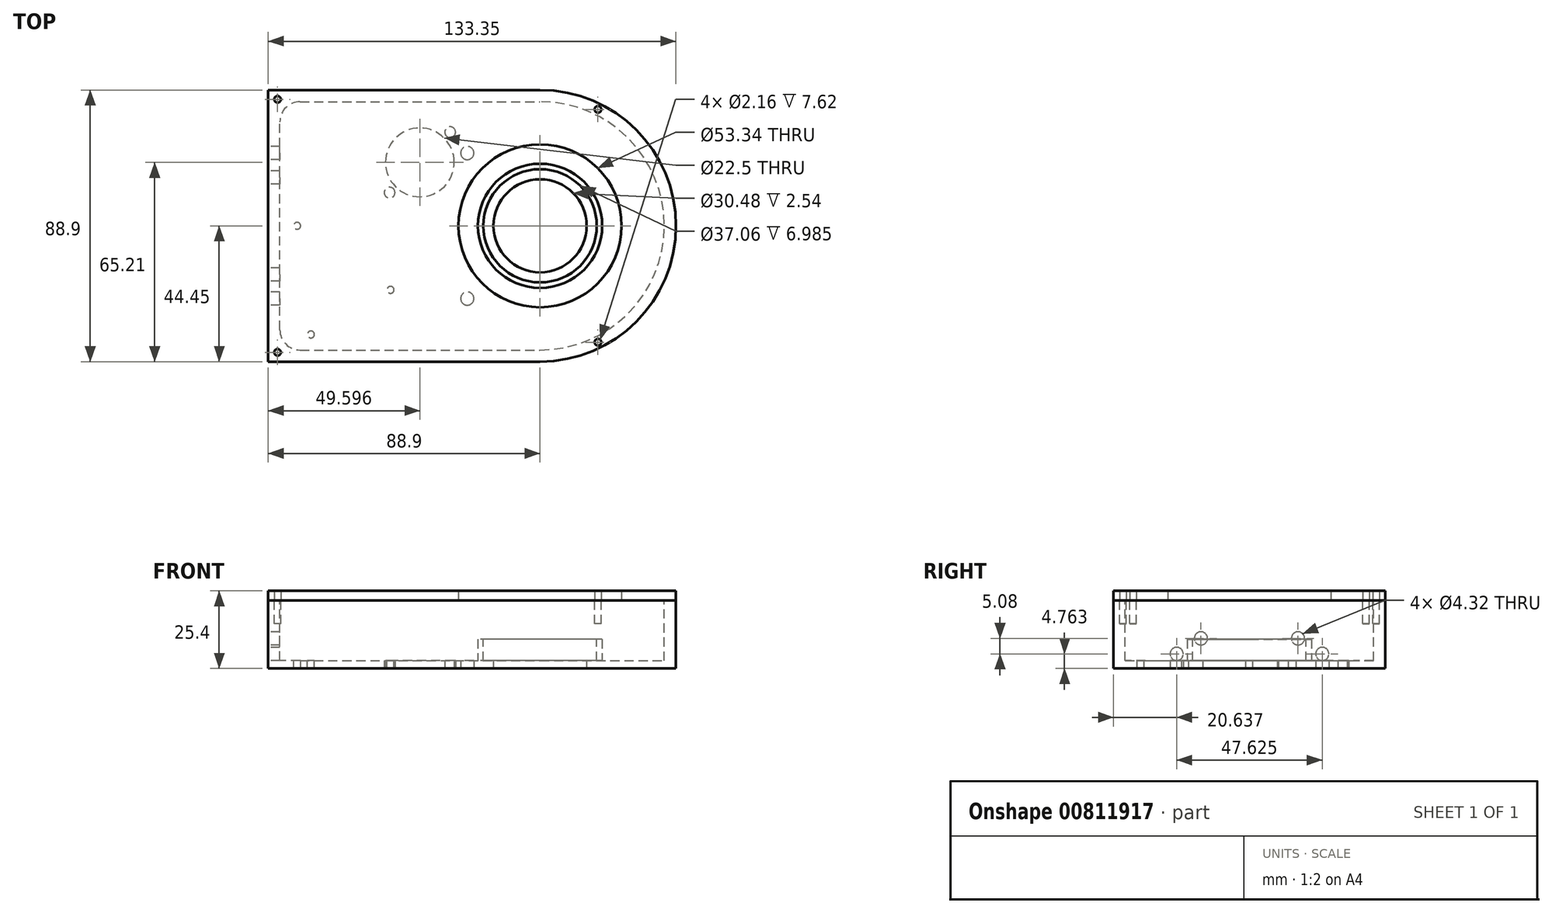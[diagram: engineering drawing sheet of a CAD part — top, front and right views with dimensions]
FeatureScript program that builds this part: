
annotation { "Feature Type Name" : "Feature", "Feature Type Description" : "" }
export const myFeature = defineFeature(function(context is Context, id is Id, definition is map)
    precondition{}
    {
        {
            var Q0;
            Q0=qCreatedBy(makeId("Top.planeOp"),FACE);
            var sketch = newSketch(context, id + "F0", { "sketchPlane" : qUnion([Q0])});
            skLineSegment(sketch, "E0.bottom", {"start": v(0, 0) * mm, "end": v(88.9, 0) * mm});
            skLineSegment(sketch, "E0.top", {"start": v(0, 88.9) * mm, "end": v(88.9, 88.9) * mm});
            skLineSegment(sketch, "E0.left", {"start": v(0, 0) * mm, "end": v(0, 88.9) * mm});
            skLineSegment(sketch, "E0.right", {"start": v(88.9, 0) * mm, "end": v(88.9, 88.9) * mm});
            skArc(sketch, "E1", {"start": v(88.9, 0) * mm, "mid": v(133.35, 44.45) * mm, "end": v(88.9, 88.9) * mm});
            skCircle(sketch, "E2", {"center": v(88.9, 44.45) * mm, "radius": 15.24 * mm});
            skCircle(sketch, "E3", {"center": v(88.9, 44.45) * mm, "radius": 31.75 * mm, "construction": true});
            skCircle(sketch, "E4", {"center": v(49.6, 65.21) * mm, "radius": 12.7 * mm, "construction": true});
            skCircle(sketch, "E5", {"center": v(49.6, 65.21) * mm, "radius": 11.25 * mm});
            skLineSegment(sketch, "E6.bottom", {"start": v(70.75, 86.36) * mm, "end": v(28.45, 86.36) * mm, "construction": true});
            skLineSegment(sketch, "E6.top", {"start": v(70.75, 44.06) * mm, "end": v(28.45, 44.06) * mm, "construction": true});
            skLineSegment(sketch, "E6.left", {"start": v(70.75, 86.36) * mm, "end": v(70.75, 44.06) * mm, "construction": true});
            skLineSegment(sketch, "E6.right", {"start": v(28.45, 86.36) * mm, "end": v(28.45, 44.06) * mm, "construction": true});
            skCircle(sketch, "E7", {"center": v(49.6, 65.21) * mm, "radius": 18 * mm, "construction": true});
            skCircle(sketch, "E8", {"center": v(88.9, 44.45) * mm, "radius": 22.23 * mm, "construction": true});
            skLineSegment(sketch, "E9", {"start": v(28.45, 44.06) * mm, "end": v(70.75, 86.36) * mm, "construction": true});
            skCircle(sketch, "E10", {"center": v(59.5, 75.1) * mm, "radius": 1.75 * mm});
            skCircle(sketch, "E11", {"center": v(39.7, 55.31) * mm, "radius": 1.75 * mm});
            skCircle(sketch, "E12", {"center": v(49.6, 65.21) * mm, "radius": 14 * mm, "construction": true});
            skSolve(sketch);
        }
        {
            var Q0;
            {var subQ4=sQuery(id+"F0.wireOp",EDGE,"E1");var subQ7=sQuery(id+"F0.wireOp",EDGE,"E0.bottom");Q0=qUnion([makeQuery(id+"F0.imprint","IMPRINT",FACE,{"disambiguationData":[TD([[makeQuery(id+"F0.imprint","IMPRINT",EDGE,{"derivedFrom":subQ7}),1.0]])]}),makeQuery(id+"F0.imprint","IMPRINT",FACE,{"disambiguationData":[TD([[makeQuery(id+"F0.imprint","IMPRINT",EDGE,{"derivedFrom":subQ4}),1.0]])]})]);}
            extrude(context, id + "F1", {"entities" : qUnion([Q0]), "depth" : 22.22 * mm});
        }
        {
            var Q0;
            Q0=makeQuery(id+"F1.opExtrude","CAP_FACE",FACE,{"disambiguationData":[OSD([sQuery(id+"F0.wireOp",EDGE,"E0.bottom"),sQuery(id+"F0.wireOp",EDGE,"E0.top"),sQuery(id+"F0.wireOp",EDGE,"E0.left"),sQuery(id+"F0.wireOp",EDGE,"E1"),sQuery(id+"F0.wireOp",EDGE,"E2")])],"isStart":false});
            var sketch = newSketch(context, id + "F2", { "sketchPlane" : qUnion([Q0])});
            skLineSegment(sketch, "E13.0", {"start": v(10.41, 85.1) * mm, "end": v(88.9, 85.1) * mm});
            skLineSegment(sketch, "E13.1", {"start": v(3.8, 10.41) * mm, "end": v(3.8, 78.49) * mm});
            skLineSegment(sketch, "E13.2", {"start": v(10.41, 3.8) * mm, "end": v(88.9, 3.8) * mm});
            skArc(sketch, "E13.3", {"start": v(88.9, 3.8) * mm, "mid": v(129.54, 44.45) * mm, "end": v(88.9, 85.1) * mm});
            skPoint(sketch, "E14.visualSharp", {"position": v(3.8, 85.1) * mm});
            skArc(sketch, "E14.filletArc", {"start": v(10.41, 85.1) * mm, "mid": v(5.74, 83.16) * mm, "end": v(3.8, 78.49) * mm});
            skPoint(sketch, "E15.visualSharp", {"position": v(3.8, 3.8) * mm});
            skArc(sketch, "E15.filletArc", {"start": v(3.8, 10.41) * mm, "mid": v(5.74, 5.74) * mm, "end": v(10.41, 3.8) * mm});
            skSolve(sketch);
        }
        {
            var Q0;
            {var subQ0=makeQuery(id+"F2.imprint","IMPRINT",EDGE,{"derivedFrom":makeQuery(id+"F1.opExtrude","CAP_EDGE",EDGE,{"disambiguationData":[OSD([sQuery(id+"F0.wireOp",EDGE,"E2")])],"isStart":false})});Q0=qUnion([makeQuery(id+"F2.imprint","IMPRINT",FACE,{"disambiguationData":[TD([[subQ0,1.0]])]}),makeQuery(id+"F2.imprint","IMPRINT",FACE,{"disambiguationData":[TD([[makeQuery(id+"F2.imprint","IMPRINT",EDGE,{"derivedFrom":sQuery(id+"F2.wireOp",EDGE,"E13.0")}),-1.0]])]})]);}
            extrude(context, id + "F3", {"entities" : qUnion([Q0]), "operationType" : NewBodyOperationType.REMOVE, "oppositeDirection" : true, "depth" : 19.68 * mm});
        }
        {
            var Q0;
            Q0=makeQuery(id+"F3.boolean.opBoolean","COPY",FACE,{"derivedFrom":makeQuery(id+"F3.opExtrude","CAP_FACE",FACE,{"disambiguationData":[OSD([sQuery(id+"F2.wireOp",EDGE,"E13.0"),sQuery(id+"F2.wireOp",EDGE,"E13.1"),sQuery(id+"F2.wireOp",EDGE,"E13.2"),sQuery(id+"F2.wireOp",EDGE,"E13.3"),sQuery(id+"F2.wireOp",EDGE,"E14.filletArc"),sQuery(id+"F2.wireOp",EDGE,"E15.filletArc")])],"isStart":false})});
            var sketch = newSketch(context, id + "F4", { "sketchPlane" : qUnion([Q0])});
            skArc(sketch, "E16.0", {"start": v(88.9, 3.8) * mm, "mid": v(129.54, 44.45) * mm, "end": v(88.9, 85.1) * mm, "construction": true});
            skCircle(sketch, "E17", {"center": v(88.9, 44.45) * mm, "radius": 20.32 * mm});
            skSolve(sketch);
        }
        {
            var Q0;
            {var subQ0=makeQuery(id+"F4.imprint","IMPRINT",EDGE,{"derivedFrom":makeQuery(id+"F3.boolean.opBoolean","INTERSECT",EDGE,{"derivedFrom":[makeQuery(id+"F1.opExtrude","SWEPT_FACE",FACE,{"disambiguationData":[OSD([sQuery(id+"F0.wireOp",EDGE,"E2")])]}),makeQuery(id+"F3.opExtrude","CAP_FACE",FACE,{"disambiguationData":[OSD([sQuery(id+"F2.wireOp",EDGE,"E13.0"),sQuery(id+"F2.wireOp",EDGE,"E13.1"),sQuery(id+"F2.wireOp",EDGE,"E13.2"),sQuery(id+"F2.wireOp",EDGE,"E13.3"),sQuery(id+"F2.wireOp",EDGE,"E14.filletArc"),sQuery(id+"F2.wireOp",EDGE,"E15.filletArc")])],"isStart":false})]})});Q0=qUnion([makeQuery(id+"F4.imprint","IMPRINT",FACE,{"disambiguationData":[TD([[subQ0,1.0]])]}),makeQuery(id+"F4.imprint","IMPRINT",FACE,{"disambiguationData":[TD([[makeQuery(id+"F4.imprint","IMPRINT",EDGE,{"derivedFrom":sQuery(id+"F4.wireOp",EDGE,"E17")}),1.0]])]})]);}
            extrude(context, id + "F5", {"entities" : qUnion([Q0]), "operationType" : NewBodyOperationType.ADD, "depth" : 7 * mm});
        }
        {
            var Q0;
            Q0=makeQuery(id+"F5.opExtrude","CAP_FACE",FACE,{"disambiguationData":[OSD([sQuery(id+"F4.wireOp",EDGE,"E17")])],"isStart":false});
            var sketch = newSketch(context, id + "F6", { "sketchPlane" : qUnion([Q0])});
            skCircle(sketch, "E18", {"center": v(88.9, 44.45) * mm, "radius": 18.53 * mm});
            skSolve(sketch);
        }
        {
            var Q0;
            Q0=makeQuery(id+"F6.imprint","IMPRINT",FACE,{"disambiguationData":[TD([[makeQuery(id+"F6.imprint","IMPRINT",EDGE,{"derivedFrom":sQuery(id+"F6.wireOp",EDGE,"E18")}),1.0]])]});
            extrude(context, id + "F7", {"entities" : qUnion([Q0]), "operationType" : NewBodyOperationType.REMOVE, "oppositeDirection" : true, "depth" : 7 * mm});
        }
        {
            var Q0;
            Q0=makeQuery(id+"F1.opExtrude","CAP_FACE",FACE,{"disambiguationData":[OSD([sQuery(id+"F0.wireOp",EDGE,"E0.bottom"),sQuery(id+"F0.wireOp",EDGE,"E0.top"),sQuery(id+"F0.wireOp",EDGE,"E0.left"),sQuery(id+"F0.wireOp",EDGE,"E1"),sQuery(id+"F0.wireOp",EDGE,"E2")])],"isStart":false});
            var sketch = newSketch(context, id + "F8", { "sketchPlane" : qUnion([Q0])});
            skLineSegment(sketch, "E19", {"start": v(3.05, 85.85) * mm, "end": v(107.83, 82.55) * mm, "construction": true});
            skLineSegment(sketch, "E20", {"start": v(107.83, 82.55) * mm, "end": v(107.83, 6.35) * mm, "construction": true});
            skLineSegment(sketch, "E21", {"start": v(107.83, 6.35) * mm, "end": v(3.05, 3.05) * mm, "construction": true});
            skCircle(sketch, "E22", {"center": v(3.05, 85.85) * mm, "radius": 1.08 * mm});
            skCircle(sketch, "E23", {"center": v(3.05, 3.05) * mm, "radius": 1.08 * mm});
            skCircle(sketch, "E24", {"center": v(107.83, 6.35) * mm, "radius": 1.08 * mm});
            skCircle(sketch, "E25", {"center": v(107.83, 82.55) * mm, "radius": 1.08 * mm});
            skSolve(sketch);
        }
        {
            var Q0;
            {Q0=qUnion([makeQuery(id+"F8.imprint","IMPRINT",FACE,{"disambiguationData":[TD([[makeQuery(id+"F8.imprint","IMPRINT",EDGE,{"derivedFrom":sQuery(id+"F8.wireOp",EDGE,"E22")}),1.0]])]}),makeQuery(id+"F8.imprint","IMPRINT",FACE,{"disambiguationData":[TD([[makeQuery(id+"F8.imprint","IMPRINT",EDGE,{"derivedFrom":sQuery(id+"F8.wireOp",EDGE,"E23")}),1.0]])]}),makeQuery(id+"F8.imprint","IMPRINT",FACE,{"disambiguationData":[TD([[makeQuery(id+"F8.imprint","IMPRINT",EDGE,{"derivedFrom":sQuery(id+"F8.wireOp",EDGE,"E24")}),1.0]])]}),makeQuery(id+"F8.imprint","IMPRINT",FACE,{"disambiguationData":[TD([[makeQuery(id+"F8.imprint","IMPRINT",EDGE,{"derivedFrom":sQuery(id+"F8.wireOp",EDGE,"E25")}),1.0]])]})]);}
            extrude(context, id + "F9", {"entities" : qUnion([Q0]), "operationType" : NewBodyOperationType.REMOVE, "oppositeDirection" : true, "depth" : 7.62 * mm});
        }
        {
            var Q0;
            Q0=makeQuery(id+"F1.opExtrude","CAP_FACE",FACE,{"disambiguationData":[OSD([sQuery(id+"F0.wireOp",EDGE,"E0.bottom"),sQuery(id+"F0.wireOp",EDGE,"E0.top"),sQuery(id+"F0.wireOp",EDGE,"E0.left"),sQuery(id+"F0.wireOp",EDGE,"E1"),sQuery(id+"F0.wireOp",EDGE,"E2")])],"isStart":false});
            var sketch = newSketch(context, id + "F10", { "sketchPlane" : qUnion([Q0])});
            skLineSegment(sketch, "E26.0", {"start": v(0, 88.9) * mm, "end": v(88.9, 88.9) * mm});
            skArc(sketch, "E27.0", {"start": v(88.9, 0) * mm, "mid": v(133.35, 44.45) * mm, "end": v(88.9, 88.9) * mm});
            skLineSegment(sketch, "E28.0", {"start": v(0, 0) * mm, "end": v(88.9, 0) * mm});
            skLineSegment(sketch, "E29.0", {"start": v(0, 0) * mm, "end": v(0, 88.9) * mm});
            skCircle(sketch, "E30", {"center": v(88.9, 44.45) * mm, "radius": 26.67 * mm});
            skCircle(sketch, "E31.0", {"center": v(3.05, 85.85) * mm, "radius": 1.08 * mm});
            skCircle(sketch, "E32.0", {"center": v(107.83, 82.55) * mm, "radius": 1.08 * mm});
            skCircle(sketch, "E33.0", {"center": v(107.83, 6.35) * mm, "radius": 1.08 * mm});
            skCircle(sketch, "E34.0", {"center": v(3.05, 3.05) * mm, "radius": 1.08 * mm});
            skSolve(sketch);
        }
        {
            var Q0;
            {Q0=qUnion([makeQuery(id+"F10.imprint","IMPRINT",FACE,{"disambiguationData":[TD([[makeQuery(id+"F10.imprint","IMPRINT",EDGE,{"derivedFrom":sQuery(id+"F10.wireOp",EDGE,"E30")}),-1.0]])]}),makeQuery(id+"F10.imprint","IMPRINT",FACE,{"disambiguationData":[TD([[makeQuery(id+"F10.imprint","IMPRINT",EDGE,{"derivedFrom":sQuery(id+"F10.wireOp",EDGE,"E26.0")}),-1.0]])]})]);}
            extrude(context, id + "F11", {"entities" : qUnion([Q0]), "depth" : 3.17 * mm});
        }
        {
            var Q0;
            Q0=makeQuery(id+"F1.opExtrude","SWEPT_FACE",FACE,{"disambiguationData":[OSD([sQuery(id+"F0.wireOp",EDGE,"E0.left")])]});
            var sketch = newSketch(context, id + "F12", { "sketchPlane" : qUnion([Q0])});
            skCircle(sketch, "E35", {"center": v(-68.26, 4.76) * mm, "radius": 2.16 * mm});
            skCircle(sketch, "E36", {"center": v(-20.64, 4.76) * mm, "radius": 2.16 * mm});
            skCircle(sketch, "E37", {"center": v(-60.33, 9.84) * mm, "radius": 2.16 * mm});
            skCircle(sketch, "E38", {"center": v(-28.58, 9.84) * mm, "radius": 2.16 * mm});
            skSolve(sketch);
        }
        {
            var Q0;
            {Q0=qUnion([makeQuery(id+"F12.imprint","IMPRINT",FACE,{"disambiguationData":[TD([[makeQuery(id+"F12.imprint","IMPRINT",EDGE,{"derivedFrom":sQuery(id+"F12.wireOp",EDGE,"E35")}),1.0]])]}),makeQuery(id+"F12.imprint","IMPRINT",FACE,{"disambiguationData":[TD([[makeQuery(id+"F12.imprint","IMPRINT",EDGE,{"derivedFrom":sQuery(id+"F12.wireOp",EDGE,"E36")}),1.0]])]}),makeQuery(id+"F12.imprint","IMPRINT",FACE,{"disambiguationData":[TD([[makeQuery(id+"F12.imprint","IMPRINT",EDGE,{"derivedFrom":sQuery(id+"F12.wireOp",EDGE,"E37")}),1.0]])]}),makeQuery(id+"F12.imprint","IMPRINT",FACE,{"disambiguationData":[TD([[makeQuery(id+"F12.imprint","IMPRINT",EDGE,{"derivedFrom":sQuery(id+"F12.wireOp",EDGE,"E38")}),1.0]])]})]);}
            var Q1;
            Q1=makeQuery(id+"F3.boolean.opBoolean","COPY",FACE,{"derivedFrom":makeQuery(id+"F3.opExtrude","SWEPT_FACE",FACE,{"disambiguationData":[OSD([sQuery(id+"F2.wireOp",EDGE,"E13.1")])]})});
            extrude(context, id + "F13", {"entities" : qUnion([Q0]), "operationType" : NewBodyOperationType.REMOVE, "endBound" : BoundingType.UP_TO_SURFACE, "oppositeDirection" : true, "endBoundEntityFace" : qUnion([Q1]), "depth" : 25.4 * mm});
        }
        {
            var Q0;
            Q0=makeQuery(id+"F1.opExtrude","CAP_FACE",FACE,{"disambiguationData":[OSD([sQuery(id+"F0.wireOp",EDGE,"E0.bottom"),sQuery(id+"F0.wireOp",EDGE,"E0.top"),sQuery(id+"F0.wireOp",EDGE,"E0.left"),sQuery(id+"F0.wireOp",EDGE,"E1"),sQuery(id+"F0.wireOp",EDGE,"E2")])],"isStart":true});
            var sketch = newSketch(context, id + "F14", { "sketchPlane" : qUnion([Q0])});
            skCircle(sketch, "E39", {"center": v(88.9, -44.45) * mm, "radius": 28.57 * mm, "construction": true});
            skLineSegment(sketch, "E40.bottom", {"start": v(60.32, -73.03) * mm, "end": v(117.47, -73.03) * mm, "construction": true});
            skLineSegment(sketch, "E40.top", {"start": v(60.32, -15.88) * mm, "end": v(117.47, -15.88) * mm, "construction": true});
            skLineSegment(sketch, "E40.left", {"start": v(60.32, -73.03) * mm, "end": v(60.32, -15.88) * mm, "construction": true});
            skLineSegment(sketch, "E40.right", {"start": v(117.47, -73.03) * mm, "end": v(117.47, -15.88) * mm, "construction": true});
            skCircle(sketch, "E41", {"center": v(65.09, -68.26) * mm, "radius": 2.16 * mm});
            skCircle(sketch, "E42", {"center": v(65.09, -20.64) * mm, "radius": 2.16 * mm});
            skSolve(sketch);
        }
        {
            var Q0;
            {Q0=qUnion([makeQuery(id+"F14.imprint","IMPRINT",FACE,{"disambiguationData":[TD([[makeQuery(id+"F14.imprint","IMPRINT",EDGE,{"derivedFrom":sQuery(id+"F14.wireOp",EDGE,"E41")}),1.0]])]}),makeQuery(id+"F14.imprint","IMPRINT",FACE,{"disambiguationData":[TD([[makeQuery(id+"F14.imprint","IMPRINT",EDGE,{"derivedFrom":sQuery(id+"F14.wireOp",EDGE,"E42")}),1.0]])]})]);}
            var Q1;
            Q1=makeQuery(id+"F11.opExtrude","CAP_FACE",FACE,{"disambiguationData":[OSD([sQuery(id+"F10.wireOp",EDGE,"E26.0"),sQuery(id+"F10.wireOp",EDGE,"E27.0"),sQuery(id+"F10.wireOp",EDGE,"E28.0"),sQuery(id+"F10.wireOp",EDGE,"E29.0"),sQuery(id+"F10.wireOp",EDGE,"E30"),sQuery(id+"F10.wireOp",EDGE,"E31.0"),sQuery(id+"F10.wireOp",EDGE,"E32.0"),sQuery(id+"F10.wireOp",EDGE,"E33.0"),sQuery(id+"F10.wireOp",EDGE,"E34.0")])],"isStart":true});
            extrude(context, id + "F15", {"entities" : qUnion([Q0]), "operationType" : NewBodyOperationType.REMOVE, "endBound" : BoundingType.UP_TO_BODY, "oppositeDirection" : true, "endBoundEntityBody" : qUnion([Q1]), "depth" : 25.4 * mm});
        }
        {
            var Q0;
            Q0=makeQuery(id+"F3.boolean.opBoolean","COPY",FACE,{"derivedFrom":makeQuery(id+"F3.opExtrude","CAP_FACE",FACE,{"disambiguationData":[OSD([sQuery(id+"F2.wireOp",EDGE,"E13.0"),sQuery(id+"F2.wireOp",EDGE,"E13.1"),sQuery(id+"F2.wireOp",EDGE,"E13.2"),sQuery(id+"F2.wireOp",EDGE,"E13.3"),sQuery(id+"F2.wireOp",EDGE,"E14.filletArc"),sQuery(id+"F2.wireOp",EDGE,"E15.filletArc")])],"isStart":false})});
            var sketch = newSketch(context, id + "F16", { "sketchPlane" : qUnion([Q0])});
            skCircle(sketch, "E43", {"center": v(9.46, 44.45) * mm, "radius": 1.13 * mm});
            skCircle(sketch, "E44", {"center": v(13.97, 8.88) * mm, "radius": 1.13 * mm});
            skCircle(sketch, "E45", {"center": v(40, 23.48) * mm, "radius": 1.13 * mm});
            skSolve(sketch);
        }
        {
            var Q0;
            Q0=qSketchRegion(id+"F16",true);
            extrude(context, id + "F17", {"entities" : qUnion([Q0]), "operationType" : NewBodyOperationType.REMOVE, "endBound" : BoundingType.THROUGH_ALL, "oppositeDirection" : true, "depth" : 25.4 * mm});
        }
    });
